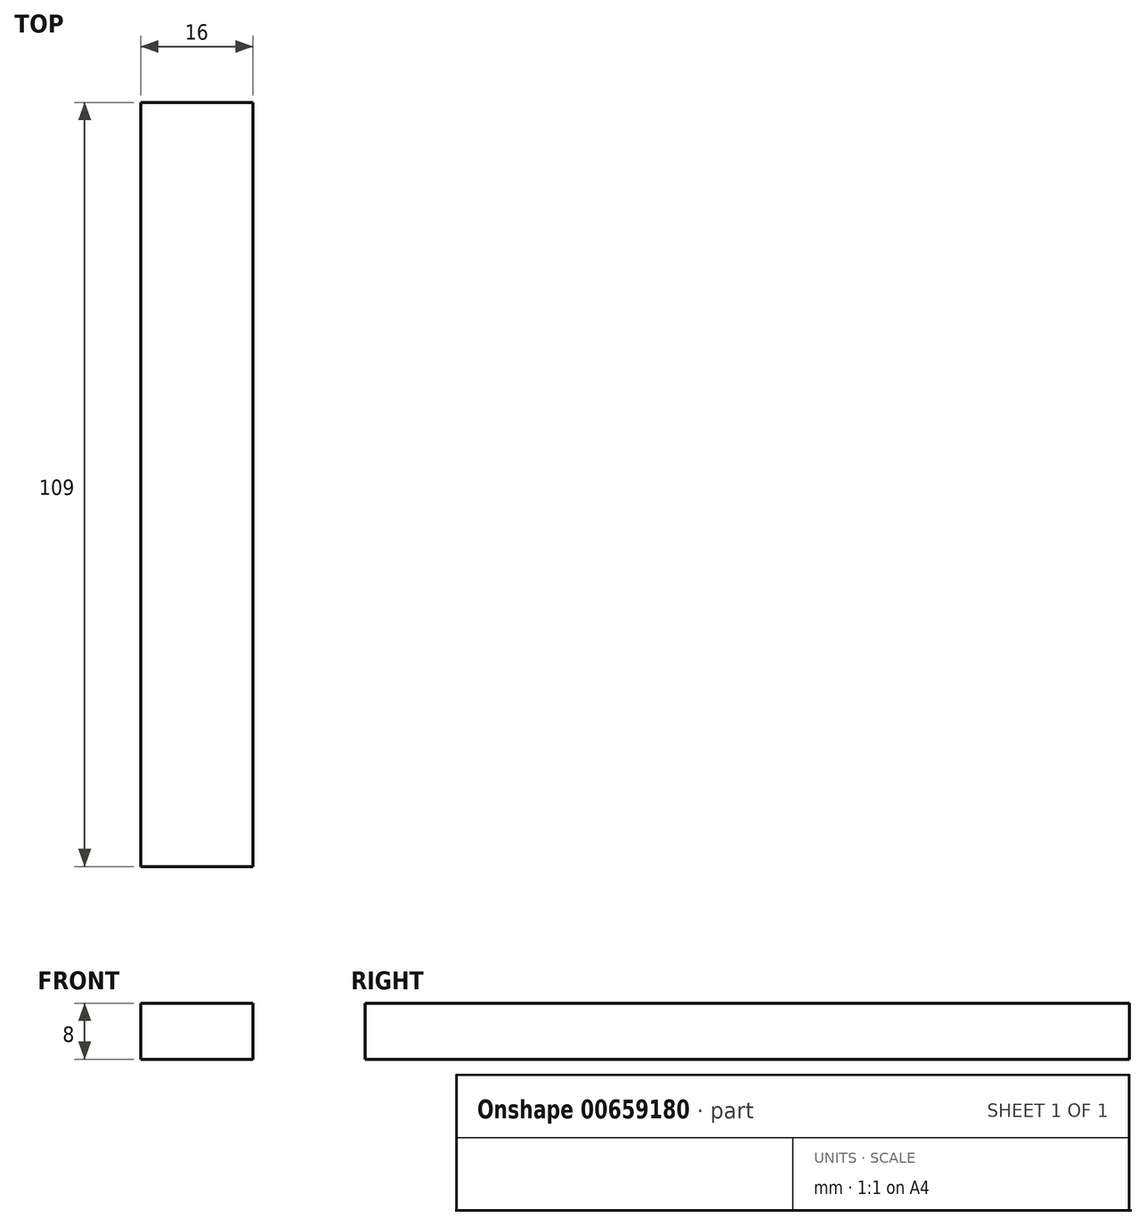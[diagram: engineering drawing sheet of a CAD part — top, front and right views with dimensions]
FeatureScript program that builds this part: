
annotation { "Feature Type Name" : "Feature", "Feature Type Description" : "" }
export const myFeature = defineFeature(function(context is Context, id is Id, definition is map)
    precondition{}
    {
        {
            var Q0;
            Q0=qCreatedBy(makeId("Front.planeOp"),FACE);
            var sketch = newSketch(context, id + "F0", { "sketchPlane" : qUnion([Q0])});
            skLineSegment(sketch, "E0.bottom", {"start": v(-8, -4) * mm, "end": v(8, -4) * mm});
            skLineSegment(sketch, "E0.top", {"start": v(-8, 4) * mm, "end": v(8, 4) * mm});
            skLineSegment(sketch, "E0.left", {"start": v(-8, -4) * mm, "end": v(-8, 4) * mm});
            skLineSegment(sketch, "E0.right", {"start": v(8, -4) * mm, "end": v(8, 4) * mm});
            skPoint(sketch, "E0.middle", {"position": v(0, 0) * mm});
            skLineSegment(sketch, "E1.bottom", {"start": v(-8, 4) * mm, "end": v(-4, 4) * mm});
            skLineSegment(sketch, "E1.top", {"start": v(-8, 8) * mm, "end": v(-4, 8) * mm});
            skLineSegment(sketch, "E1.left", {"start": v(-8, 4) * mm, "end": v(-8, 8) * mm});
            skLineSegment(sketch, "E1.right", {"start": v(-4, 4) * mm, "end": v(-4, 8) * mm});
            skSolve(sketch);
        }
        {
            var Q0;
            Q0=makeQuery(id+"F0.imprint","IMPRINT",FACE,{"disambiguationData":[TD([[makeQuery(id+"F0.imprint","IMPRINT",EDGE,{"derivedFrom":sQuery(id+"F0.wireOp",EDGE,"E1.bottom")}),1.0]])]});
            var Q1;
            Q1=makeQuery(id+"F0.imprint","IMPRINT",FACE,{"disambiguationData":[TD([[makeQuery(id+"F0.imprint","IMPRINT",EDGE,{"derivedFrom":sQuery(id+"F0.wireOp",EDGE,"E0.bottom")}),1.0]])]});
            extrude(context, id + "F1", {"entities" : qUnion([Q0, Q1]), "endBound" : BoundingType.SYMMETRIC, "depth" : 109 * mm, "offsetDistance" : 25 * mm});
        }
    });
